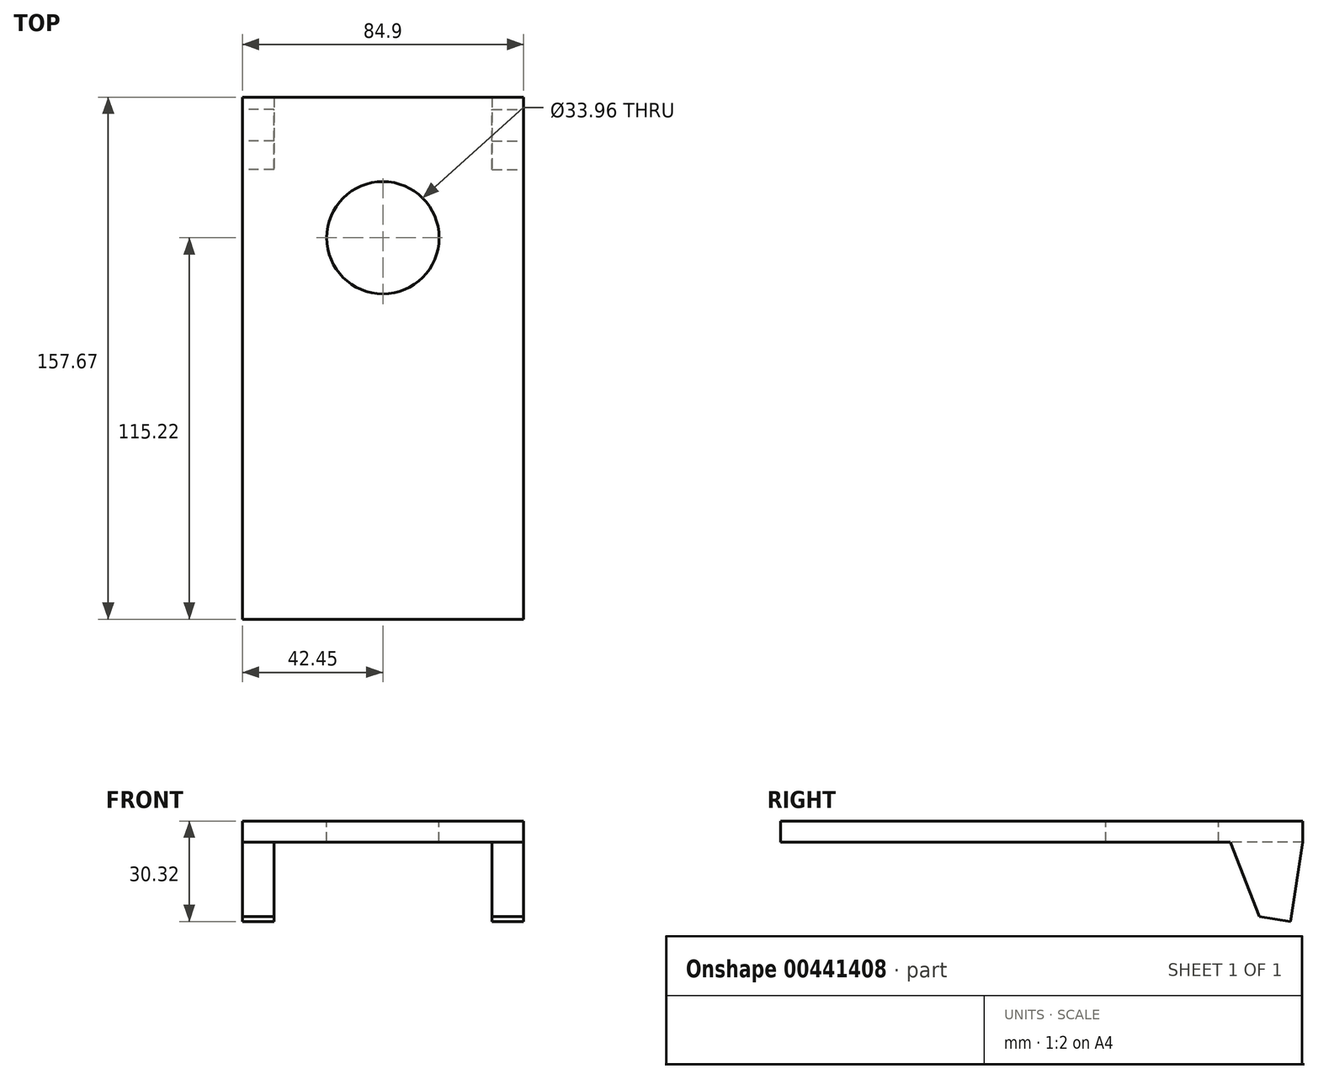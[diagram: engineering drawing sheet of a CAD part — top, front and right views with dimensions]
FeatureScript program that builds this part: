
annotation { "Feature Type Name" : "Feature", "Feature Type Description" : "" }
export const myFeature = defineFeature(function(context is Context, id is Id, definition is map)
    precondition{}
    {
        {
            var Q0;
            Q0=qCreatedBy(makeId("Top.planeOp"),FACE);
            var sketch = newSketch(context, id + "F0", { "sketchPlane" : qUnion([Q0])});
            skLineSegment(sketch, "E0.bottom", {"start": v(-42.45, 42.45) * mm, "end": v(42.45, 42.45) * mm});
            skLineSegment(sketch, "E0.top", {"start": v(-42.45, -115.22) * mm, "end": v(42.45, -115.22) * mm});
            skLineSegment(sketch, "E0.left", {"start": v(-42.45, 42.45) * mm, "end": v(-42.45, -115.22) * mm});
            skLineSegment(sketch, "E0.right", {"start": v(42.45, 42.45) * mm, "end": v(42.45, -115.22) * mm});
            skLineSegment(sketch, "E1", {"start": v(0, 42.45) * mm, "end": v(0, -115.22) * mm, "construction": true});
            skLineSegment(sketch, "E2", {"start": v(-42.45, 0) * mm, "end": v(42.45, 0) * mm, "construction": true});
            skPoint(sketch, "E3", {"position": v(0, 0) * mm});
            skCircle(sketch, "E4", {"center": v(0, 0) * mm, "radius": 16.98 * mm});
            skSolve(sketch);
        }
        {
            var Q0;
            Q0 = qSketchRegion(id + "F0", true);
            extrude(context, id + "F1", {"entities" : qUnion([Q0]), "oppositeDirection" : true, "depth" : 6.35 * mm});
        }
        {
            var Q0;
            Q0=makeQuery(id+"F1.opExtrude","SWEPT_FACE",FACE,{"disambiguationData":[OSD([sQuery(id+"F0.wireOp",EDGE,"E0.left")])]});
            var sketch = newSketch(context, id + "F2", { "sketchPlane" : qUnion([Q0])});
            skLineSegment(sketch, "E5", {"start": v(-42.45, -6.35) * mm, "end": v(-38.72, -30.32) * mm});
            skLineSegment(sketch, "E6", {"start": v(-38.72, -30.32) * mm, "end": v(115.22, -6.35) * mm, "construction": true});
            skLineSegment(sketch, "E7", {"start": v(115.22, -6.35) * mm, "end": v(-42.45, -6.35) * mm, "construction": true});
            skLineSegment(sketch, "E8", {"start": v(-42.45, -6.35) * mm, "end": v(-20.6, -6.35) * mm});
            skLineSegment(sketch, "E9", {"start": v(-20.6, -6.35) * mm, "end": v(-29.3, -28.85) * mm});
            skLineSegment(sketch, "E10", {"start": v(-29.3, -28.85) * mm, "end": v(-38.72, -30.32) * mm});
            skSolve(sketch);
        }
        {
            var Q0;
            Q0=makeQuery(id+"F2.imprint","IMPRINT",FACE,{"disambiguationData":[TD([[makeQuery(id+"F2.imprint","IMPRINT",EDGE,{"derivedFrom":sQuery(id+"F2.wireOp",EDGE,"E5")}),1.0]])]});
            extrude(context, id + "F3", {"entities" : qUnion([Q0]), "operationType" : NewBodyOperationType.ADD, "oppositeDirection" : true, "depth" : 9.52 * mm});
        }
        {
            var Q0;
            Q0=makeQuery(id+"F1.opExtrude","SWEPT_FACE",FACE,{"disambiguationData":[OSD([sQuery(id+"F0.wireOp",EDGE,"E0.right")])]});
            var sketch = newSketch(context, id + "F4", { "sketchPlane" : qUnion([Q0])});
            skLineSegment(sketch, "E11", {"start": v(42.45, -6.35) * mm, "end": v(20.6, -6.35) * mm});
            skLineSegment(sketch, "E12", {"start": v(20.6, -6.35) * mm, "end": v(29.3, -28.85) * mm});
            skLineSegment(sketch, "E13", {"start": v(42.45, -6.35) * mm, "end": v(38.72, -30.32) * mm});
            skLineSegment(sketch, "E14", {"start": v(29.3, -28.85) * mm, "end": v(38.72, -30.32) * mm});
            skSolve(sketch);
        }
        {
            var Q0;
            Q0 = qSketchRegion(id + "F4", true);
            extrude(context, id + "F5", {"entities" : qUnion([Q0]), "operationType" : NewBodyOperationType.ADD, "oppositeDirection" : true, "depth" : 9.52 * mm});
        }
    });
